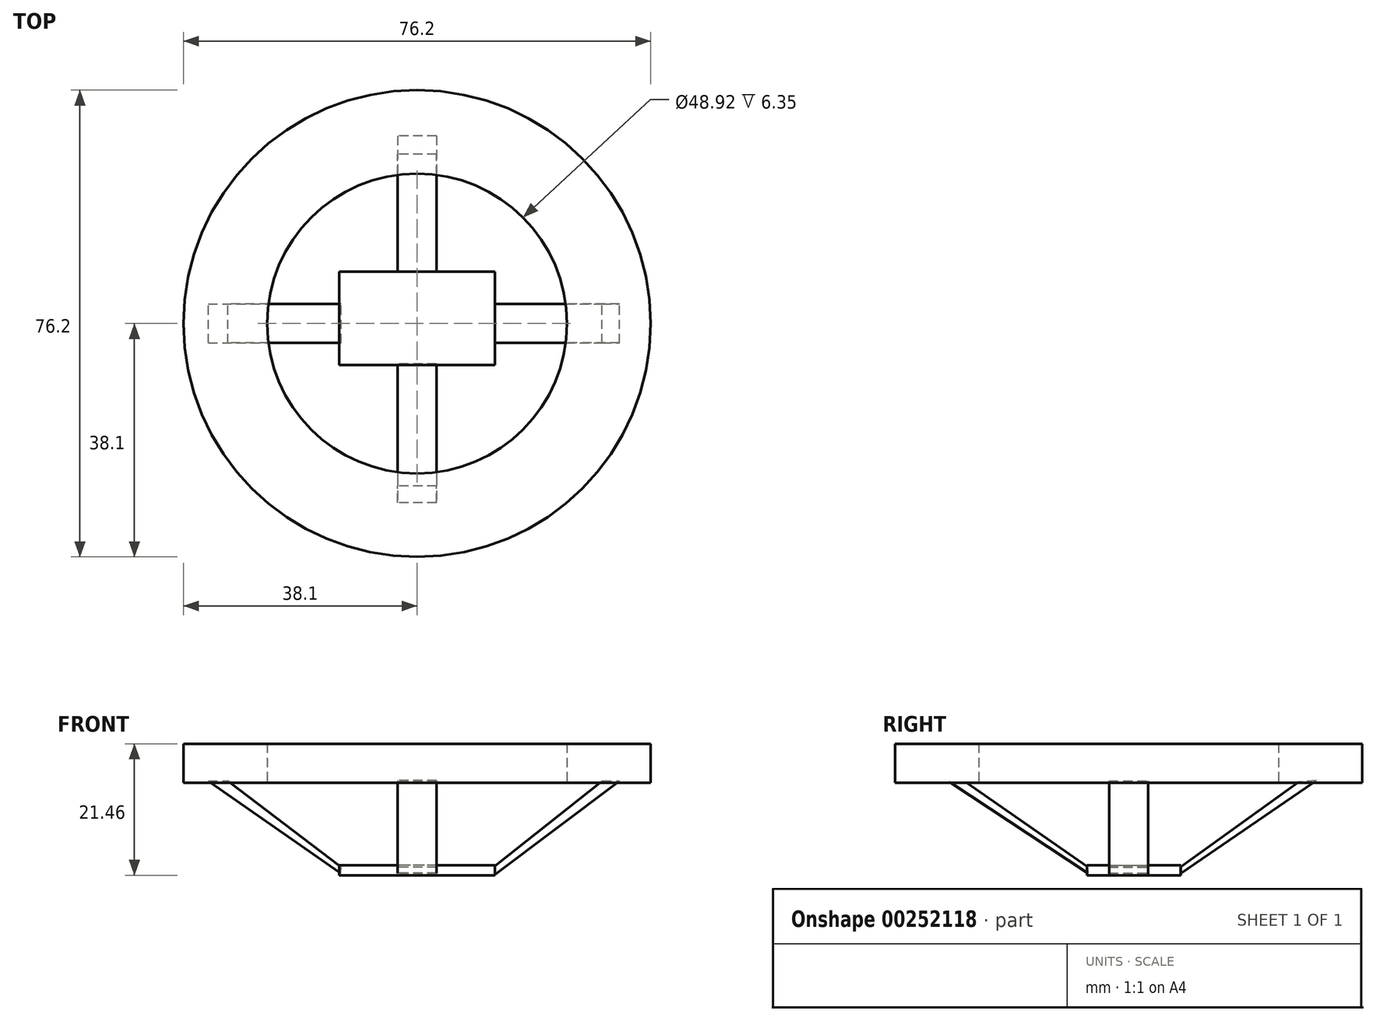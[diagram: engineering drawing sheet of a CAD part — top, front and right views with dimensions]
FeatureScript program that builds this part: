
annotation { "Feature Type Name" : "Feature", "Feature Type Description" : "" }
export const myFeature = defineFeature(function(context is Context, id is Id, definition is map)
    precondition{}
    {
        {
            var Q0;
            Q0=qCreatedBy(makeId("Top.planeOp"),FACE);
            var sketch = newSketch(context, id + "F0", { "sketchPlane" : qUnion([Q0])});
            skCircle(sketch, "E0", {"center": v(0, 0) * mm, "radius": 38.1 * mm});
            skCircle(sketch, "E1", {"center": v(0, 0) * mm, "radius": 24.46 * mm});
            skSolve(sketch);
        }
        {
            var Q0;
            Q0 = qSketchRegion(id + "F0", true);
            extrude(context, id + "F1", {"entities" : qUnion([Q0]), "endBound" : BoundingType.SYMMETRIC, "depth" : 6.35 * mm});
        }
        {
            var Q0;
            Q0=qCreatedBy(makeId("Right.planeOp"),FACE);
            var sketch = newSketch(context, id + "F2", { "sketchPlane" : qUnion([Q0])});
            skLineSegment(sketch, "E2.bottom", {"start": v(-6.75, -16.68) * mm, "end": v(8.5, -16.68) * mm});
            skLineSegment(sketch, "E2.top", {"start": v(-6.75, -18.28) * mm, "end": v(8.5, -18.28) * mm});
            skLineSegment(sketch, "E2.left", {"start": v(-6.75, -16.68) * mm, "end": v(-6.75, -18.28) * mm});
            skLineSegment(sketch, "E2.right", {"start": v(8.5, -16.68) * mm, "end": v(8.5, -18.28) * mm});
            skSolve(sketch);
        }
        {
            var Q0;
            Q0 = qSketchRegion(id + "F2", true);
            extrude(context, id + "F3", {"entities" : qUnion([Q0]), "endBound" : BoundingType.SYMMETRIC, "depth" : 25.4 * mm});
        }
        {
            var Q0;
            Q0=qCreatedBy(makeId("Right.planeOp"),FACE);
            var sketch = newSketch(context, id + "F4", { "sketchPlane" : qUnion([Q0])});
            skLineSegment(sketch, "E3", {"start": v(8.4, -16.97) * mm, "end": v(27.67, -3.1) * mm});
            skLineSegment(sketch, "E4", {"start": v(-6.63, -16.96) * mm, "end": v(-26.51, -3.1) * mm});
            skLineSegment(sketch, "E5", {"start": v(-6.6, -17.95) * mm, "end": v(-6.63, -16.96) * mm});
            skLineSegment(sketch, "E6", {"start": v(-6.6, -17.95) * mm, "end": v(-29.25, -3.02) * mm});
            skLineSegment(sketch, "E7", {"start": v(-29.25, -3.02) * mm, "end": v(-26.51, -3.1) * mm});
            skLineSegment(sketch, "E8", {"start": v(30.62, -2.83) * mm, "end": v(8.42, -18.02) * mm});
            skLineSegment(sketch, "E9", {"start": v(8.42, -18.02) * mm, "end": v(8.4, -16.97) * mm});
            skLineSegment(sketch, "E10", {"start": v(30.62, -2.83) * mm, "end": v(27.67, -3.1) * mm});
            skSolve(sketch);
        }
        {
            var Q0;
            Q0=qCreatedBy(makeId("Front.planeOp"),FACE);
            var sketch = newSketch(context, id + "F5", { "sketchPlane" : qUnion([Q0])});
            skLineSegment(sketch, "E11", {"start": v(-12.4, -16.96) * mm, "end": v(-30.86, -2.89) * mm});
            skLineSegment(sketch, "E12", {"start": v(11.87, -17.92) * mm, "end": v(30.7, -2.5) * mm});
            skLineSegment(sketch, "E13", {"start": v(-34.06, -2.89) * mm, "end": v(-30.86, -2.89) * mm});
            skLineSegment(sketch, "E14", {"start": v(-34.06, -2.89) * mm, "end": v(-12.45, -17.95) * mm});
            skLineSegment(sketch, "E15", {"start": v(-12.45, -17.95) * mm, "end": v(-12.4, -16.96) * mm});
            skLineSegment(sketch, "E16", {"start": v(27.55, -2.89) * mm, "end": v(30.7, -2.5) * mm});
            skLineSegment(sketch, "E17", {"start": v(27.55, -2.89) * mm, "end": v(12.12, -16.96) * mm});
            skSolve(sketch);
        }
        {
            var Q0;
            Q0=makeQuery(id+"F5.imprint","IMPRINT",FACE,{"disambiguationData":[TD([[makeQuery(id+"F5.imprint","IMPRINT",EDGE,{"derivedFrom":sQuery(id+"F5.wireOp",EDGE,"E11")}),1.0]])]});
            extrude(context, id + "F6", {"entities" : qUnion([Q0]), "endBound" : BoundingType.SYMMETRIC, "depth" : 6.35 * mm});
        }
        {
            var Q0;
            Q0=qCreatedBy(makeId("Front.planeOp"),FACE);
            var sketch = newSketch(context, id + "F7", { "sketchPlane" : qUnion([Q0])});
            skLineSegment(sketch, "E18", {"start": v(12.67, -16.8) * mm, "end": v(30.18, -2.89) * mm});
            skLineSegment(sketch, "E19", {"start": v(30.18, -2.89) * mm, "end": v(33.02, -2.89) * mm});
            skLineSegment(sketch, "E20", {"start": v(33.02, -2.89) * mm, "end": v(12.67, -18.23) * mm});
            skLineSegment(sketch, "E21", {"start": v(12.67, -18.23) * mm, "end": v(12.67, -16.8) * mm});
            skSolve(sketch);
        }
        {
            var Q0;
            Q0=makeQuery(id+"F7.imprint","IMPRINT",FACE,{"disambiguationData":[TD([[makeQuery(id+"F7.imprint","IMPRINT",EDGE,{"derivedFrom":sQuery(id+"F7.wireOp",EDGE,"E18")}),-1.0]])]});
            extrude(context, id + "F8", {"entities" : qUnion([Q0]), "endBound" : BoundingType.SYMMETRIC, "depth" : 6.35 * mm});
        }
        {
            var Q0;
            Q0=makeQuery(id+"F4.imprint","IMPRINT",FACE,{"disambiguationData":[TD([[makeQuery(id+"F4.imprint","IMPRINT",EDGE,{"derivedFrom":sQuery(id+"F4.wireOp",EDGE,"E4")}),1.0]])]});
            extrude(context, id + "F9", {"entities" : qUnion([Q0]), "endBound" : BoundingType.SYMMETRIC, "depth" : 6.35 * mm});
        }
        {
            var Q0;
            Q0=makeQuery(id+"F4.imprint","IMPRINT",FACE,{"disambiguationData":[TD([[makeQuery(id+"F4.imprint","IMPRINT",EDGE,{"derivedFrom":sQuery(id+"F4.wireOp",EDGE,"E3")}),-1.0]])]});
            extrude(context, id + "F10", {"entities" : qUnion([Q0]), "endBound" : BoundingType.SYMMETRIC, "depth" : 6.35 * mm});
        }
    });
